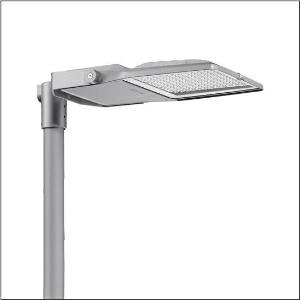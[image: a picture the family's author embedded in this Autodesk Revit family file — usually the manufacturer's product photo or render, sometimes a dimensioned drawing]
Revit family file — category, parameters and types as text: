
# Revit family: floodlight_fl_21_midi___pl52_5xa7786e2d3a_7127
name_source: partatom
category: Lighting Fixtures
units: mm (PartAtom-declared; Revit-internal decimal feet)

## family parameters
Cut with Voids When Loaded = No
Host = Face
Light Source = No
Part Type = Normal
Room Calculation Point = No
Round Connector Dimension = Use Diameter
Shared = No

## types (1)
- --- (1 x LED, 26940 lm, 212.4 W, 3000K)
    Apparent Load = 212 VA
    CIE Flux Codes = 26 60 98 100 100
    Color Rendering = 70
    Color Temperature = 3000K
    Default Elevation = 1800 mm
    Description = Floodlight FL 21 midi, floodlight, primary light control with lens, of PMMA, primary optical cover: protective disc, of toughened safety glass, transparent, light distribution: PL52, light emission: direct distribution, installation type: surface-mounted, LED, High Power LED, rated luminous flux: 26.940lm, luminous efficacy: 127lm/W, light colour: 730, colour temperature: 3000K, control gear: ECG Smart Interface, control: flexible luminous flux parameterisation, time-dependent luminous flux control, constant luminous flux control, overheat protection, pre-setting: logarithmic dimming characteristic, with terminal, 6-pole, mains connection: 220..240V, AC, 50/60Hz, start of lifetime: 212W, end of service life: 231W, reduction: 95W, luminaire housing, of diecast aluminium, powder-coated, Siteco® metallic grey (DB 702S), corrosivity category C5 mid according to DIN EN ISO 12944, sealing non-destructively replaceable, please order mast flange separately, mast bracket, of steel, galvanised, powder-coated, Siteco® metallic grey (DB 702S), Smart Interface below and above, protection rating (complete): IP66, insulation class (complete): insulation class II (safety insulation), certification: CE, ENEC, VDE, protection symbol: D, impact resistance: IK08, permissible operating ambient temperature: -40..+40°C, permissible operating ambient temperature for outdoor applications: -40..+50°C, standard: DIN EN 12944, LABS conformity tested according to VDMA 24364:2018-05, packaging unit: 1 piece

Light Distribution: PL52
    Height = 76 mm
    Lamp = 1 x LED
    Lamp Light Flux = 26940 lm
    Lamp Power = 212.4 W
    Lamp count = 1
    Length = 657 mm
    Luminous efficacy = 127 lm/W
    Manufacturer = Siteco
    ModVariant = No
    Model = 5XA7786E2D3A
    Number of Poles = 1
    OnlyDefault = Yes
    Power Factor = 1
    Product Name = Floodlight FL 21 midi | PL52
    Product group = floodlight | pylon annexe
    ProductGroupID = 6200
    Protection Class = Protection class II
    Protection Degree = IP 66
    RLX_Detail_Level = 1
    RLX_Emergency_Light_Flux = 0 lm
    RLX_Emergency_Type = 0
    RLX_Emergency_Type_DB = No
    RlxData = <blob elided: 153609 chars, md5=2ee1f9f0>
    Socket = socket
    Standby Power = 0 W
    System Light Flux = 26940 lm
    System Power = 212 W
    Type Comments = factory setting: luminous flux: 100 % | dim-lin: 254 | 710 mA
    Type Image = l_1007123.jpg
    URL = http://relux.com
    VarID = @adj_148839
    Voltage = 0 V
    Weight = 0.00 kg
    Width = 442 mm

## geometry (parser evidence)
native form markers: Blend x4, Sweep x13
no freeform markers — native parametric forms only
